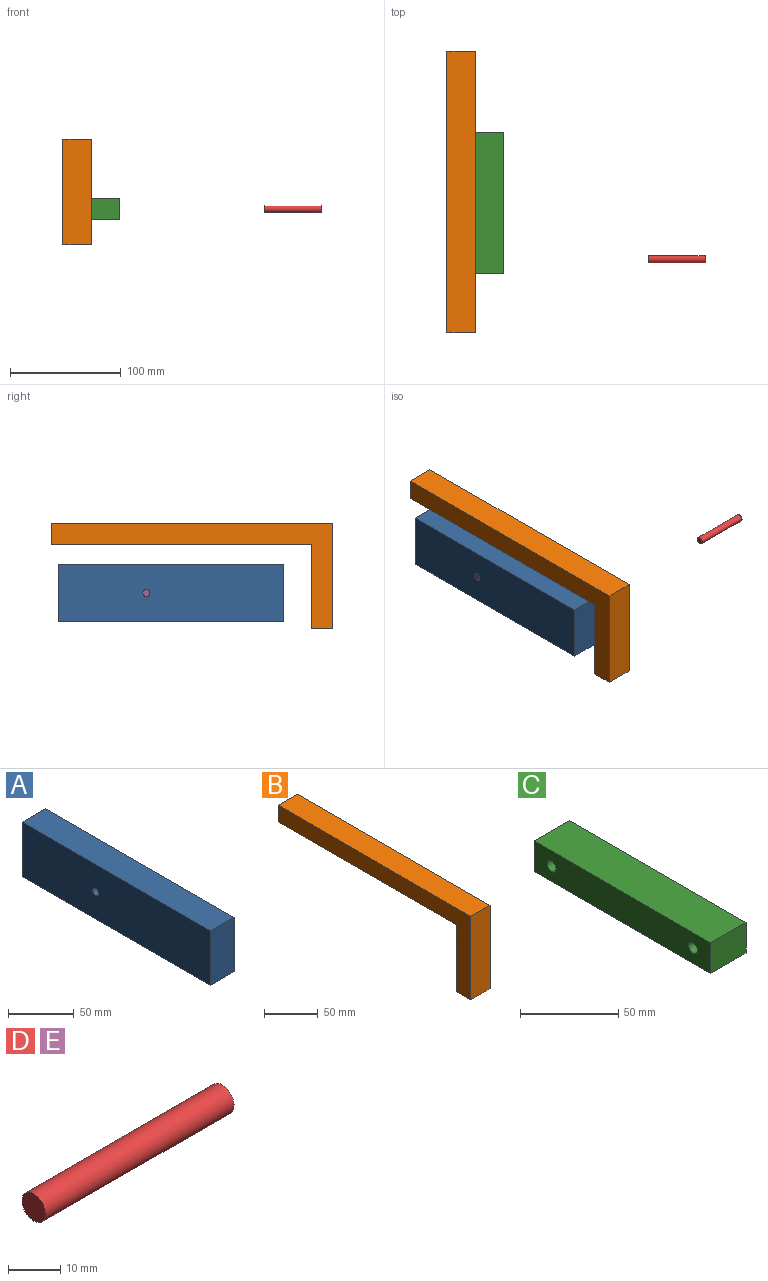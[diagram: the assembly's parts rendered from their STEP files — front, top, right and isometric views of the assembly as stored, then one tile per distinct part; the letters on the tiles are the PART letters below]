
ASSEMBLY  parts=5 mates=9
PART A: 7 faces, bbox 25.4x203.2x50.8 mm
  f0: plane 203.2x25.4mm, normal (0,0,1), area 5161.3mm2, adj f1,f4,f5,f6
  f1: plane 50.8x25.4mm, normal (0,-1,0), area 1290.3mm2, adj f0,f2,f5,f6
  f2: plane 203.2x25.4mm, normal (0,0,-1), area 5161.3mm2, adj f1,f4,f5,f6
  f3: cylinder r=3.17mm len=25.4mm, axis (-1,0,0), area 506.7mm2, adj f5,f6
  f4: plane 50.8x25.4mm, normal (0,1,0), area 1290.3mm2, adj f0,f2,f5,f6
  f5: plane 203.2x50.8mm, normal (1,0,0), area 10290.9mm2, adj f0,f1,f2,f3,f4
  f6: plane 203.2x50.8mm, normal (-1,0,0), area 10290.9mm2, adj f0,f1,f2,f3,f4
PART B: 8 faces, bbox 25.4x254x95.3 mm
  f0: plane 25.4x19.05mm, normal (0,0,-1), area 483.9mm2, adj f1,f5,f6,f7
  f1: plane 76.2x25.4mm, normal (0,1,0), area 1935.5mm2, adj f0,f2,f6,f7
  f2: plane 234.95x25.4mm, normal (0,0,-1), area 5967.7mm2, adj f1,f3,f6,f7
  f3: plane 25.4x19.05mm, normal (0,1,0), area 483.9mm2, adj f2,f4,f6,f7
  f4: plane 254x25.4mm, normal (0,0,1), area 6451.6mm2, adj f3,f5,f6,f7
  f5: plane 95.25x25.4mm, normal (0,-1,0), area 2419.3mm2, adj f0,f4,f6,f7
  f6: plane 254x95.25mm, normal (1,0,0), area 6290.3mm2, adj f0,f1,f2,f3,f4,f5
  f7: plane 254x95.25mm, normal (-1,0,0), area 6290.3mm2, adj f0,f1,f2,f3,f4,f5
PART C: 8 faces, bbox 25.4x127x19.1 mm
  f0: plane 127x25.4mm, normal (0,0,1), area 3225.8mm2, adj f1,f5,f6,f7
  f1: plane 25.4x19.05mm, normal (0,-1,0), area 483.9mm2, adj f0,f2,f6,f7
  f2: plane 127x25.4mm, normal (0,0,-1), area 3225.8mm2, adj f1,f5,f6,f7
  f3: cylinder r=3.17mm len=25.4mm, axis (-1,0,0), area 506.7mm2, adj f6,f7
  f4: cylinder r=3.17mm len=25.4mm, axis (-1,0,0), area 506.7mm2, adj f6,f7
  f5: plane 25.4x19.05mm, normal (0,1,0), area 483.9mm2, adj f0,f2,f6,f7
  f6: plane 127x19.05mm, normal (1,0,0), area 2356mm2, adj f0,f1,f2,f3,f4,f5
  f7: plane 127x19.05mm, normal (-1,0,0), area 2356mm2, adj f0,f1,f2,f3,f4,f5
PART D: 3 faces, bbox 50.8x6.4x6.4 mm
  f0: cylinder r=3.17mm len=50.8mm, axis (-1,0,0), area 1013.4mm2, adj f1,f2
  f1: plane 6.35x6.35mm, normal (1,0,0), area 31.7mm2, adj f0
  f2: plane 6.35x6.35mm, normal (-1,0,0), area 31.7mm2, adj f0
PART E: same geometry as D
PLACE A t=(-57.57,166.62,52.28)mm
PLACE B t=(-57.57,147.68,45.48)mm fixed
PLACE C t=(-32.17,138.04,52.28)mm
PLACE D t=(124.3,87.24,52.28)mm
PLACE E t=(-57.57,188.84,52.28)mm
MATE planar E.f0 <-> C.f6  axis (1,0,0) through (-6.77,188.84,52.28)mm
MATE slider C.f4 <-> E.f0  axis (1,0,0) through (-6.77,188.84,52.28)mm
MATE planar B.f6 <-> A.f5  axis (1,0,0) through (-32.17,39.73,20.08)mm
MATE parallel B.f6 <-> A.f5  axis (1,0,0) through (-32.17,120.57,94.82)mm
MATE parallel A.f0 <-> B.f4  axis (0,0,1) through (-44.87,166.62,77.68)mm
MATE slider A.f3 <-> E.f0  axis (1,0,0) through (-32.17,188.84,52.28)mm
MATE slider C.f3 <-> D.f0  axis (-1,0,0) through (-6.77,87.24,52.28)mm
MATE planar A.f3 <-> E.f0  axis (-1,0,0) through (-57.57,188.84,52.28)mm
MATE parallel A.f1 <-> B.f5  axis (0,-1,0) through (-44.87,65.02,52.28)mm
